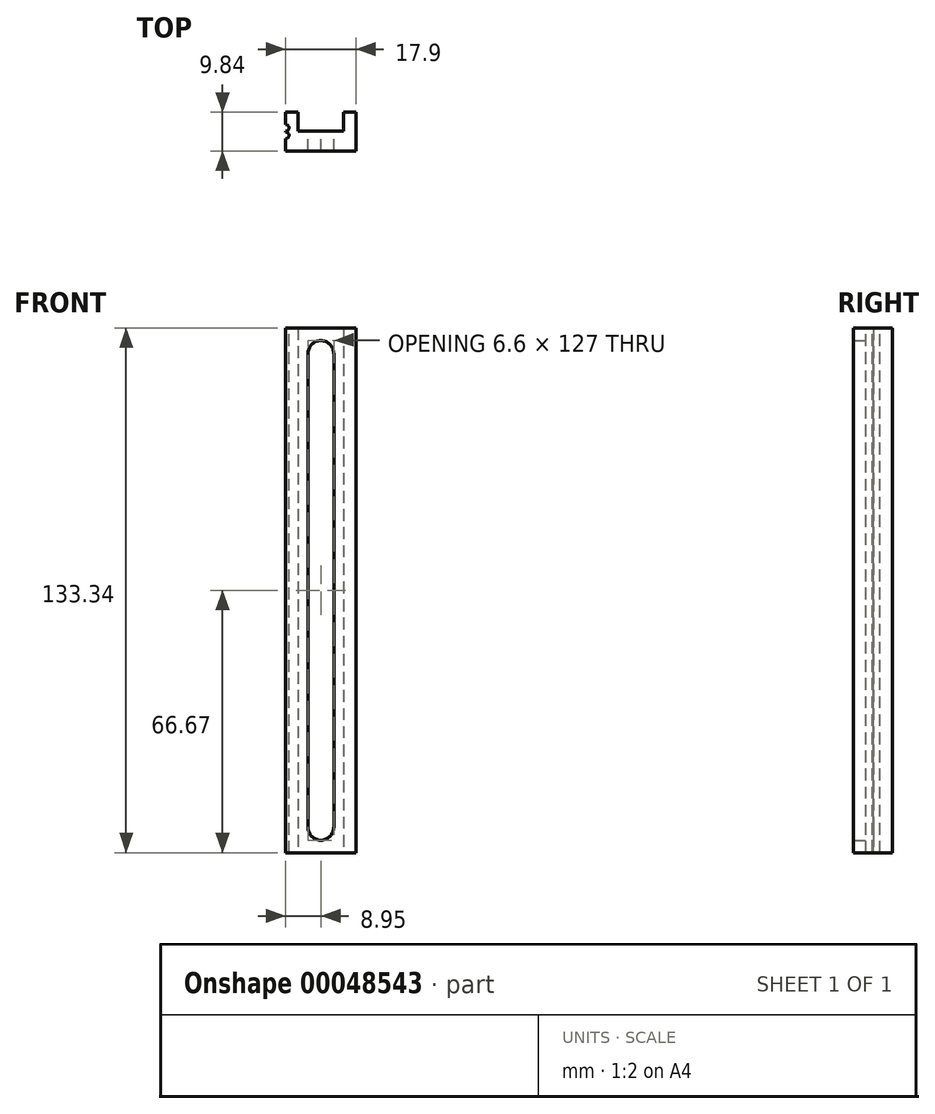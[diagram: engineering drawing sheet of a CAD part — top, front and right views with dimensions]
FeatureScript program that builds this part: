
annotation { "Feature Type Name" : "Feature", "Feature Type Description" : "" }
export const myFeature = defineFeature(function(context is Context, id is Id, definition is map)
    precondition{}
    {
        {
            var Q0;
            Q0=qCreatedBy(makeId("Front.planeOp"),FACE);
            var sketch = newSketch(context, id + "F0", { "sketchPlane" : qUnion([Q0])});
            skLineSegment(sketch, "E0.rect.bottom", {"start": v(-8.95, -66.68) * mm, "end": v(8.95, -66.68) * mm});
            skLineSegment(sketch, "E0.rect.top", {"start": v(-8.95, 66.68) * mm, "end": v(8.95, 66.68) * mm});
            skLineSegment(sketch, "E0.rect.left", {"start": v(-8.95, -66.68) * mm, "end": v(-8.95, 66.68) * mm});
            skLineSegment(sketch, "E0.rect.right", {"start": v(8.95, -66.68) * mm, "end": v(8.95, 66.68) * mm});
            skPoint(sketch, "E0.rect.middle", {"position": v(0, 0) * mm});
            skLineSegment(sketch, "E1.rect.bottom", {"start": v(-3.3, -63.5) * mm, "end": v(3.3, -63.5) * mm});
            skLineSegment(sketch, "E1.rect.top", {"start": v(-3.3, 63.5) * mm, "end": v(3.3, 63.5) * mm});
            skLineSegment(sketch, "E1.rect.left", {"start": v(-3.3, -63.5) * mm, "end": v(-3.3, 63.5) * mm});
            skLineSegment(sketch, "E1.rect.right", {"start": v(3.3, -63.5) * mm, "end": v(3.3, 63.5) * mm});
            skLineSegment(sketch, "E2.bottom", {"start": v(-8.95, 66.68) * mm, "end": v(-5.78, 66.68) * mm});
            skLineSegment(sketch, "E2.top", {"start": v(-8.95, -66.68) * mm, "end": v(-5.78, -66.68) * mm});
            skLineSegment(sketch, "E2.left", {"start": v(-8.95, 66.68) * mm, "end": v(-8.95, -66.68) * mm});
            skLineSegment(sketch, "E2.right", {"start": v(-5.78, 66.68) * mm, "end": v(-5.78, -66.68) * mm});
            skLineSegment(sketch, "E3.bottom", {"start": v(8.95, 66.68) * mm, "end": v(5.78, 66.68) * mm});
            skLineSegment(sketch, "E3.top", {"start": v(8.95, -66.68) * mm, "end": v(5.78, -66.68) * mm});
            skLineSegment(sketch, "E3.left", {"start": v(8.95, 66.68) * mm, "end": v(8.95, -66.68) * mm});
            skLineSegment(sketch, "E3.right", {"start": v(5.78, 66.68) * mm, "end": v(5.78, -66.68) * mm});
            skSolve(sketch);
        }
        {
            var Q0;
            Q0=makeQuery(id+"F0.imprint","IMPRINT",FACE,{"disambiguationData":[TD([[makeQuery(id+"F0.imprint","IMPRINT",EDGE,{"derivedFrom":sQuery(id+"F0.wireOp",EDGE,"E1.rect.bottom")}),-1.0]])]});
            var Q1;
            {var subQ2=sQuery(id+"F0.wireOp",EDGE,"E0.rect.left");Q1=makeQuery(id+"F0.imprint","IMPRINT",FACE,{"disambiguationData":[TD([[makeQuery(id+"F0.imprint","IMPRINT",EDGE,{"derivedFrom":subQ2}),-1.0]])]});}
            var Q2;
            {var subQ0=sQuery(id+"F0.wireOp",EDGE,"E0.rect.right");Q2=makeQuery(id+"F0.imprint","IMPRINT",FACE,{"disambiguationData":[TD([[makeQuery(id+"F0.imprint","IMPRINT",EDGE,{"derivedFrom":subQ0}),1.0]])]});}
            extrude(context, id + "F1", {"entities" : qUnion([Q0, Q1, Q2]), "depth" : 5.08 * mm});
        }
        {
            var Q0;
            Q0=makeQuery(id+"F1.opExtrude","SWEPT_EDGE",EDGE,{"disambiguationData":[OSD([sQuery(id+"F0.wireOp",EDGE,"E1.rect.top"),sQuery(id+"F0.wireOp",EDGE,"E1.rect.right")])]});
            var Q1;
            Q1=makeQuery(id+"F1.opExtrude","SWEPT_EDGE",EDGE,{"disambiguationData":[OSD([sQuery(id+"F0.wireOp",EDGE,"E1.rect.top"),sQuery(id+"F0.wireOp",EDGE,"E1.rect.left")])]});
            var Q2;
            Q2=makeQuery(id+"F1.opExtrude","SWEPT_EDGE",EDGE,{"disambiguationData":[OSD([sQuery(id+"F0.wireOp",EDGE,"E1.rect.bottom"),sQuery(id+"F0.wireOp",EDGE,"E1.rect.left")])]});
            var Q3;
            Q3=makeQuery(id+"F1.opExtrude","SWEPT_EDGE",EDGE,{"disambiguationData":[OSD([sQuery(id+"F0.wireOp",EDGE,"E1.rect.bottom"),sQuery(id+"F0.wireOp",EDGE,"E1.rect.right")])]});
            fillet(context, id + "F2", {"entities" : qUnion([Q0, Q1, Q2, Q3]), "radius" : 3.43 * mm, "tangentPropagation" : true, "allowEdgeOverflow" : false});
        }
        {
            var Q0;
            {var subQ0=sQuery(id+"F0.wireOp",EDGE,"E0.rect.right");Q0=makeQuery(id+"F0.imprint","IMPRINT",FACE,{"disambiguationData":[TD([[makeQuery(id+"F0.imprint","IMPRINT",EDGE,{"derivedFrom":subQ0}),1.0]])]});}
            var Q1;
            {var subQ2=sQuery(id+"F0.wireOp",EDGE,"E0.rect.left");Q1=makeQuery(id+"F0.imprint","IMPRINT",FACE,{"disambiguationData":[TD([[makeQuery(id+"F0.imprint","IMPRINT",EDGE,{"derivedFrom":subQ2}),-1.0]])]});}
            extrude(context, id + "F3", {"entities" : qUnion([Q0, Q1]), "operationType" : NewBodyOperationType.ADD, "oppositeDirection" : true, "depth" : 4.76 * mm});
        }
        {
            var Q0;
            {var subQ0=sQuery(id+"F0.wireOp",EDGE,"E0.rect.top");Q0=makeQuery(id+"F3.boolean.opBoolean","MERGE",FACE,{"derivedFrom":[makeQuery(id+"F1.opExtrude","SWEPT_FACE",FACE,{"disambiguationData":[OSD([subQ0])]}),makeQuery(id+"F3.opExtrude","SWEPT_FACE",FACE,{"disambiguationData":[OSD([subQ0]),TDD([makeQuery(id+"F0.imprint","IMPRINT",EDGE,{"disambiguationData":[TD([[makeQuery(id+"F0.imprint","INTERSECT",VERTEX,{"derivedFrom":[subQ0,sQuery(id+"F0.wireOp",EDGE,"E0.rect.right")]}),1.0]])],"derivedFrom":subQ0})])]}),makeQuery(id+"F3.opExtrude","SWEPT_FACE",FACE,{"disambiguationData":[OSD([subQ0]),TDD([makeQuery(id+"F0.imprint","IMPRINT",EDGE,{"disambiguationData":[TD([[makeQuery(id+"F0.imprint","INTERSECT",VERTEX,{"derivedFrom":[subQ0,sQuery(id+"F0.wireOp",EDGE,"E2.right")]}),1.0]])],"derivedFrom":subQ0})])]})]});}
            var sketch = newSketch(context, id + "F4", { "sketchPlane" : qUnion([Q0])});
            skCircle(sketch, "E4", {"center": v(-8.95, 0.8) * mm, "radius": 0.86 * mm});
            skCircle(sketch, "E5", {"center": v(-8.95, -1.11) * mm, "radius": 0.86 * mm});
            skLineSegment(sketch, "E6", {"start": v(0, 0) * mm, "end": v(0, -5.08) * mm, "construction": true});
            skCircle(sketch, "E7.MirrorC", {"center": v(8.95, 0.8) * mm, "radius": 0.86 * mm});
            skCircle(sketch, "E8.MirrorC", {"center": v(8.95, -1.11) * mm, "radius": 0.86 * mm});
            skSolve(sketch);
        }
        {
            var Q0;
            {var subQ0=sQuery(id+"F4.wireOp",EDGE,"E4");var subQ1=sQuery(id+"F0.wireOp",EDGE,"E0.rect.left");var subQ2=sQuery(id+"F0.wireOp",EDGE,"E0.rect.top");var subQ3=makeQuery(id+"F3.boolean.opBoolean","MERGE",EDGE,{"derivedFrom":[makeQuery(id+"F1.opExtrude","SWEPT_EDGE",EDGE,{"disambiguationData":[OSD([subQ2,subQ1])]}),makeQuery(id+"F3.opExtrude","SWEPT_EDGE",EDGE,{"disambiguationData":[OSD([subQ2,subQ1])]})]});var subQ4=makeQuery(id+"F4.imprint","INTERSECT",VERTEX,{"disambiguationData":[OD(0.0)],"derivedFrom":[subQ3,subQ0]});Q0=makeQuery(id+"F4.imprint","IMPRINT",FACE,{"disambiguationData":[TD([[makeQuery(id+"F4.imprint","IMPRINT",EDGE,{"disambiguationData":[TD([[subQ4,1.0]])],"derivedFrom":subQ0}),1.0]])]});}
            var Q1;
            {var subQ0=sQuery(id+"F4.wireOp",EDGE,"E5");var subQ1=sQuery(id+"F0.wireOp",EDGE,"E0.rect.left");var subQ2=sQuery(id+"F0.wireOp",EDGE,"E0.rect.top");var subQ3=makeQuery(id+"F3.boolean.opBoolean","MERGE",EDGE,{"derivedFrom":[makeQuery(id+"F1.opExtrude","SWEPT_EDGE",EDGE,{"disambiguationData":[OSD([subQ2,subQ1])]}),makeQuery(id+"F3.opExtrude","SWEPT_EDGE",EDGE,{"disambiguationData":[OSD([subQ2,subQ1])]})]});var subQ4=makeQuery(id+"F4.imprint","INTERSECT",VERTEX,{"disambiguationData":[OD(0.0)],"derivedFrom":[subQ3,subQ0]});Q1=makeQuery(id+"F4.imprint","IMPRINT",FACE,{"disambiguationData":[TD([[makeQuery(id+"F4.imprint","IMPRINT",EDGE,{"disambiguationData":[TD([[subQ4,-1.0]])],"derivedFrom":subQ0}),1.0]])]});}
            var Q2;
            {var subQ0=sQuery(id+"F4.wireOp",EDGE,"E8.MirrorC");var subQ1=sQuery(id+"F0.wireOp",EDGE,"E0.rect.right");var subQ2=sQuery(id+"F0.wireOp",EDGE,"E0.rect.top");var subQ3=makeQuery(id+"F3.boolean.opBoolean","MERGE",EDGE,{"derivedFrom":[makeQuery(id+"F1.opExtrude","SWEPT_EDGE",EDGE,{"disambiguationData":[OSD([subQ2,subQ1])]}),makeQuery(id+"F3.opExtrude","SWEPT_EDGE",EDGE,{"disambiguationData":[OSD([subQ2,subQ1])]})]});var subQ4=makeQuery(id+"F4.imprint","INTERSECT",VERTEX,{"disambiguationData":[OD(0.0)],"derivedFrom":[subQ3,subQ0]});Q2=makeQuery(id+"F4.imprint","IMPRINT",FACE,{"disambiguationData":[TD([[makeQuery(id+"F4.imprint","IMPRINT",EDGE,{"disambiguationData":[TD([[subQ4,-1.0]])],"derivedFrom":subQ0}),-1.0]])]});}
            var Q3;
            {var subQ0=sQuery(id+"F4.wireOp",EDGE,"E7.MirrorC");var subQ1=sQuery(id+"F0.wireOp",EDGE,"E0.rect.right");var subQ2=sQuery(id+"F0.wireOp",EDGE,"E0.rect.top");var subQ3=makeQuery(id+"F3.boolean.opBoolean","MERGE",EDGE,{"derivedFrom":[makeQuery(id+"F1.opExtrude","SWEPT_EDGE",EDGE,{"disambiguationData":[OSD([subQ2,subQ1])]}),makeQuery(id+"F3.opExtrude","SWEPT_EDGE",EDGE,{"disambiguationData":[OSD([subQ2,subQ1])]})]});var subQ4=makeQuery(id+"F4.imprint","INTERSECT",VERTEX,{"disambiguationData":[OD(0.0)],"derivedFrom":[subQ3,subQ0]});Q3=makeQuery(id+"F4.imprint","IMPRINT",FACE,{"disambiguationData":[TD([[makeQuery(id+"F4.imprint","IMPRINT",EDGE,{"disambiguationData":[TD([[subQ4,1.0]])],"derivedFrom":subQ0}),-1.0]])]});}
            extrude(context, id + "F5", {"entities" : qUnion([Q0, Q1, Q2, Q3]), "operationType" : NewBodyOperationType.REMOVE, "endBound" : BoundingType.THROUGH_ALL, "oppositeDirection" : true, "depth" : 25.4 * mm});
        }
    });
